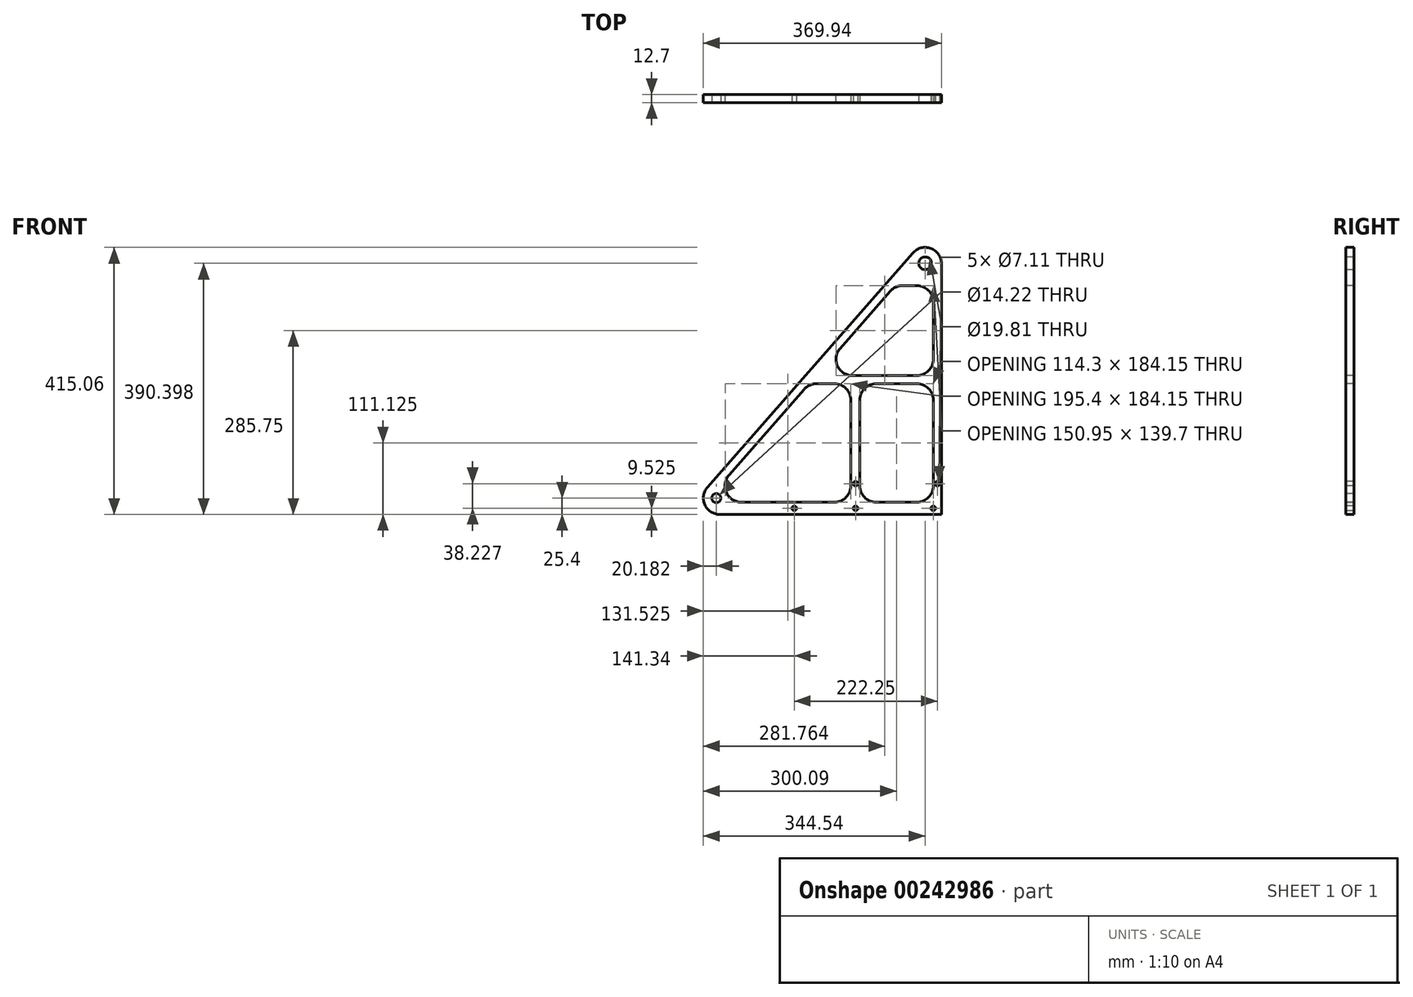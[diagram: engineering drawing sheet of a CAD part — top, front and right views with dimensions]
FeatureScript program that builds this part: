
annotation { "Feature Type Name" : "Feature", "Feature Type Description" : "" }
export const myFeature = defineFeature(function(context is Context, id is Id, definition is map)
    precondition{}
    {
        {
            var Q0;
            Q0=qCreatedBy(makeId("Front.planeOp"),FACE);
            var sketch = newSketch(context, id + "F0", { "sketchPlane" : qUnion([Q0])});
            skLineSegment(sketch, "E0", {"start": v(0, 0) * mm, "end": v(0, 457.2) * mm});
            skLineSegment(sketch, "E1", {"start": v(0, 457.2) * mm, "end": v(-400.56, 0) * mm});
            skLineSegment(sketch, "E2", {"start": v(-400.56, 0) * mm, "end": v(0, 0) * mm});
            skSolve(sketch);
        }
        {
            var Q0;
            Q0 = qSketchRegion(id + "F0", true);
            extrude(context, id + "F1", {"entities" : qUnion([Q0]), "depth" : 12.7 * mm});
        }
        {
            var Q0;
            Q0=makeQuery(id+"F1.opExtrude","CAP_FACE",FACE,{"disambiguationData":[OSD([sQuery(id+"F0.wireOp",EDGE,"E0"),sQuery(id+"F0.wireOp",EDGE,"E1"),sQuery(id+"F0.wireOp",EDGE,"E2")])],"isStart":false});
            var sketch = newSketch(context, id + "F2", { "sketchPlane" : qUnion([Q0])});
            skLineSegment(sketch, "E3.bottom", {"start": v(-127, 203.2) * mm, "end": v(-12.7, 203.2) * mm});
            skLineSegment(sketch, "E3.top", {"start": v(-127, 19.05) * mm, "end": v(-12.7, 19.05) * mm});
            skLineSegment(sketch, "E3.left", {"start": v(-127, 203.2) * mm, "end": v(-127, 19.05) * mm});
            skLineSegment(sketch, "E3.right", {"start": v(-12.7, 203.2) * mm, "end": v(-12.7, 19.05) * mm});
            skLineSegment(sketch, "E4", {"start": v(-366.98, 19.05) * mm, "end": v(-140.72, 19.05) * mm});
            skLineSegment(sketch, "E5", {"start": v(-140.72, 19.05) * mm, "end": v(-140.72, 203.2) * mm});
            skLineSegment(sketch, "E6", {"start": v(-72.13, 355.6) * mm, "end": v(-194.52, 215.9) * mm});
            skLineSegment(sketch, "E7", {"start": v(-72.13, 355.6) * mm, "end": v(-12.7, 355.6) * mm});
            skLineSegment(sketch, "E8", {"start": v(-194.52, 215.9) * mm, "end": v(-12.7, 215.9) * mm});
            skLineSegment(sketch, "E9", {"start": v(-12.7, 215.9) * mm, "end": v(-12.7, 355.6) * mm});
            skLineSegment(sketch, "E10", {"start": v(-366.98, 19.05) * mm, "end": v(-205.65, 203.2) * mm});
            skLineSegment(sketch, "E11", {"start": v(-140.72, 203.2) * mm, "end": v(-205.65, 203.2) * mm});
            skPoint(sketch, "E12", {"position": v(-25.4, 390.4) * mm});
            skPoint(sketch, "E13", {"position": v(-12.7, 9.53) * mm});
            skPoint(sketch, "E14", {"position": v(-6.35, 47.75) * mm});
            skPoint(sketch, "E15", {"position": v(-133.35, 9.52) * mm});
            skPoint(sketch, "E16", {"position": v(-133.35, 47.75) * mm});
            skPoint(sketch, "E17", {"position": v(-228.6, 9.52) * mm});
            skPoint(sketch, "E18", {"position": v(-349.76, 25.4) * mm});
            skSolve(sketch);
        }
        {
            var Q0;
            Q0 = qSketchRegion(id + "F2", true);
            var Q1;
            Q1=makeQuery(id+"F1.opExtrude","CAP_FACE",FACE,{"disambiguationData":[OSD([sQuery(id+"F0.wireOp",EDGE,"E0"),sQuery(id+"F0.wireOp",EDGE,"E1"),sQuery(id+"F0.wireOp",EDGE,"E2")])],"isStart":true});
            extrude(context, id + "F3", {"entities" : qUnion([Q0]), "operationType" : NewBodyOperationType.REMOVE, "endBound" : BoundingType.UP_TO_SURFACE, "oppositeDirection" : true, "endBoundEntityFace" : qUnion([Q1]), "depth" : 25.4 * mm});
        }
        {
            var Q0;
            Q0=makeQuery(id+"F3.boolean.opBoolean","COPY",EDGE,{"derivedFrom":makeQuery(id+"F3.opExtrude","SWEPT_EDGE",EDGE,{"disambiguationData":[OSD([sQuery(id+"F2.wireOp",EDGE,"E10"),sQuery(id+"F2.wireOp",EDGE,"E11")])]})});
            var Q1;
            Q1=makeQuery(id+"F3.boolean.opBoolean","COPY",EDGE,{"derivedFrom":makeQuery(id+"F3.opExtrude","SWEPT_EDGE",EDGE,{"disambiguationData":[OSD([sQuery(id+"F2.wireOp",EDGE,"E5"),sQuery(id+"F2.wireOp",EDGE,"E11")])]})});
            var Q2;
            Q2=makeQuery(id+"F3.boolean.opBoolean","COPY",EDGE,{"derivedFrom":makeQuery(id+"F3.opExtrude","SWEPT_EDGE",EDGE,{"disambiguationData":[OSD([sQuery(id+"F2.wireOp",EDGE,"E3.bottom"),sQuery(id+"F2.wireOp",EDGE,"E3.left")])]})});
            var Q3;
            Q3=makeQuery(id+"F3.boolean.opBoolean","COPY",EDGE,{"derivedFrom":makeQuery(id+"F3.opExtrude","SWEPT_EDGE",EDGE,{"disambiguationData":[OSD([sQuery(id+"F2.wireOp",EDGE,"E3.bottom"),sQuery(id+"F2.wireOp",EDGE,"E3.right")])]})});
            var Q4;
            Q4=makeQuery(id+"F3.boolean.opBoolean","COPY",EDGE,{"derivedFrom":makeQuery(id+"F3.opExtrude","SWEPT_EDGE",EDGE,{"disambiguationData":[OSD([sQuery(id+"F2.wireOp",EDGE,"E7"),sQuery(id+"F2.wireOp",EDGE,"E9")])]})});
            var Q5;
            Q5=makeQuery(id+"F3.boolean.opBoolean","COPY",EDGE,{"derivedFrom":makeQuery(id+"F3.opExtrude","SWEPT_EDGE",EDGE,{"disambiguationData":[OSD([sQuery(id+"F2.wireOp",EDGE,"E6"),sQuery(id+"F2.wireOp",EDGE,"E7")])]})});
            var Q6;
            Q6=makeQuery(id+"F3.boolean.opBoolean","COPY",EDGE,{"derivedFrom":makeQuery(id+"F3.opExtrude","SWEPT_EDGE",EDGE,{"disambiguationData":[OSD([sQuery(id+"F2.wireOp",EDGE,"E4"),sQuery(id+"F2.wireOp",EDGE,"E10")])]})});
            var Q7;
            Q7=makeQuery(id+"F3.boolean.opBoolean","COPY",EDGE,{"derivedFrom":makeQuery(id+"F3.opExtrude","SWEPT_EDGE",EDGE,{"disambiguationData":[OSD([sQuery(id+"F2.wireOp",EDGE,"E4"),sQuery(id+"F2.wireOp",EDGE,"E5")])]})});
            var Q8;
            Q8=makeQuery(id+"F3.boolean.opBoolean","COPY",EDGE,{"derivedFrom":makeQuery(id+"F3.opExtrude","SWEPT_EDGE",EDGE,{"disambiguationData":[OSD([sQuery(id+"F2.wireOp",EDGE,"E3.top"),sQuery(id+"F2.wireOp",EDGE,"E3.left")])]})});
            var Q9;
            Q9=makeQuery(id+"F3.boolean.opBoolean","COPY",EDGE,{"derivedFrom":makeQuery(id+"F3.opExtrude","SWEPT_EDGE",EDGE,{"disambiguationData":[OSD([sQuery(id+"F2.wireOp",EDGE,"E3.top"),sQuery(id+"F2.wireOp",EDGE,"E3.right")])]})});
            var Q10;
            Q10=makeQuery(id+"F3.boolean.opBoolean","COPY",EDGE,{"derivedFrom":makeQuery(id+"F3.opExtrude","SWEPT_EDGE",EDGE,{"disambiguationData":[OSD([sQuery(id+"F2.wireOp",EDGE,"E6"),sQuery(id+"F2.wireOp",EDGE,"E8")])]})});
            var Q11;
            Q11=makeQuery(id+"F3.boolean.opBoolean","COPY",EDGE,{"derivedFrom":makeQuery(id+"F3.opExtrude","SWEPT_EDGE",EDGE,{"disambiguationData":[OSD([sQuery(id+"F2.wireOp",EDGE,"E8"),sQuery(id+"F2.wireOp",EDGE,"E9")])]})});
            fillet(context, id + "F4", {"entities" : qUnion([Q0, Q1, Q2, Q3, Q4, Q5, Q6, Q7, Q8, Q9, Q10, Q11]), "radius" : 25.4 * mm, "tangentPropagation" : true, "allowEdgeOverflow" : false});
        }
        {
            var Q0;
            Q0=sQuery(id+"F2.wireOp",VERTEX,"E18");
            var Q1;
            Q1=makeQuery(id+"F1.opExtrude","SWEPT_BODY",BODY,{"disambiguationData":[OSD([sQuery(id+"F0.wireOp",EDGE,"E0"),sQuery(id+"F0.wireOp",EDGE,"E1"),sQuery(id+"F0.wireOp",EDGE,"E2")])]});
            hole(context, id + "F5", {"style" : HoleStyle.SIMPLE, "endStyle" : HoleEndStyle.THROUGH, "holeDiameter" : 14.22 * mm, "startFromSketch" : true, "locations" : qUnion([Q0]), "scope" : qUnion([Q1]), "isTappedThrough" : true});
        }
        {
            var Q0;
            Q0=sQuery(id+"F2.wireOp",VERTEX,"E12");
            var Q1;
            Q1=makeQuery(id+"F1.opExtrude","SWEPT_BODY",BODY,{"disambiguationData":[OSD([sQuery(id+"F0.wireOp",EDGE,"E0"),sQuery(id+"F0.wireOp",EDGE,"E1"),sQuery(id+"F0.wireOp",EDGE,"E2")])]});
            hole(context, id + "F6", {"style" : HoleStyle.SIMPLE, "endStyle" : HoleEndStyle.THROUGH, "holeDiameter" : 19.8 * mm, "startFromSketch" : true, "locations" : qUnion([Q0]), "scope" : qUnion([Q1]), "isTappedThrough" : true});
        }
        {
            var Q0;
            Q0=sQuery(id+"F2.wireOp",VERTEX,"E17");
            var Q1;
            Q1=sQuery(id+"F2.wireOp",VERTEX,"E15");
            var Q2;
            Q2=sQuery(id+"F2.wireOp",VERTEX,"E16");
            var Q3;
            Q3=sQuery(id+"F2.wireOp",VERTEX,"E14");
            var Q4;
            Q4=sQuery(id+"F2.wireOp",VERTEX,"E13");
            var Q5;
            Q5=makeQuery(id+"F1.opExtrude","SWEPT_BODY",BODY,{"disambiguationData":[OSD([sQuery(id+"F0.wireOp",EDGE,"E0"),sQuery(id+"F0.wireOp",EDGE,"E1"),sQuery(id+"F0.wireOp",EDGE,"E2")])]});
            hole(context, id + "F7", {"style" : HoleStyle.SIMPLE, "endStyle" : HoleEndStyle.THROUGH, "holeDiameter" : 7.11 * mm, "startFromSketch" : true, "locations" : qUnion([Q0, Q1, Q2, Q3, Q4]), "scope" : qUnion([Q5]), "isTappedThrough" : true});
        }
        {
            var Q0;
            Q0=makeQuery(id+"F1.opExtrude","SWEPT_EDGE",EDGE,{"disambiguationData":[OSD([sQuery(id+"F0.wireOp",EDGE,"E0"),sQuery(id+"F0.wireOp",EDGE,"E1")])]});
            var Q1;
            Q1=makeQuery(id+"F1.opExtrude","SWEPT_EDGE",EDGE,{"disambiguationData":[OSD([sQuery(id+"F0.wireOp",EDGE,"E1"),sQuery(id+"F0.wireOp",EDGE,"E2")])]});
            fillet(context, id + "F8", {"entities" : qUnion([Q0, Q1]), "radius" : 25.4 * mm, "tangentPropagation" : true, "allowEdgeOverflow" : false});
        }
    });
